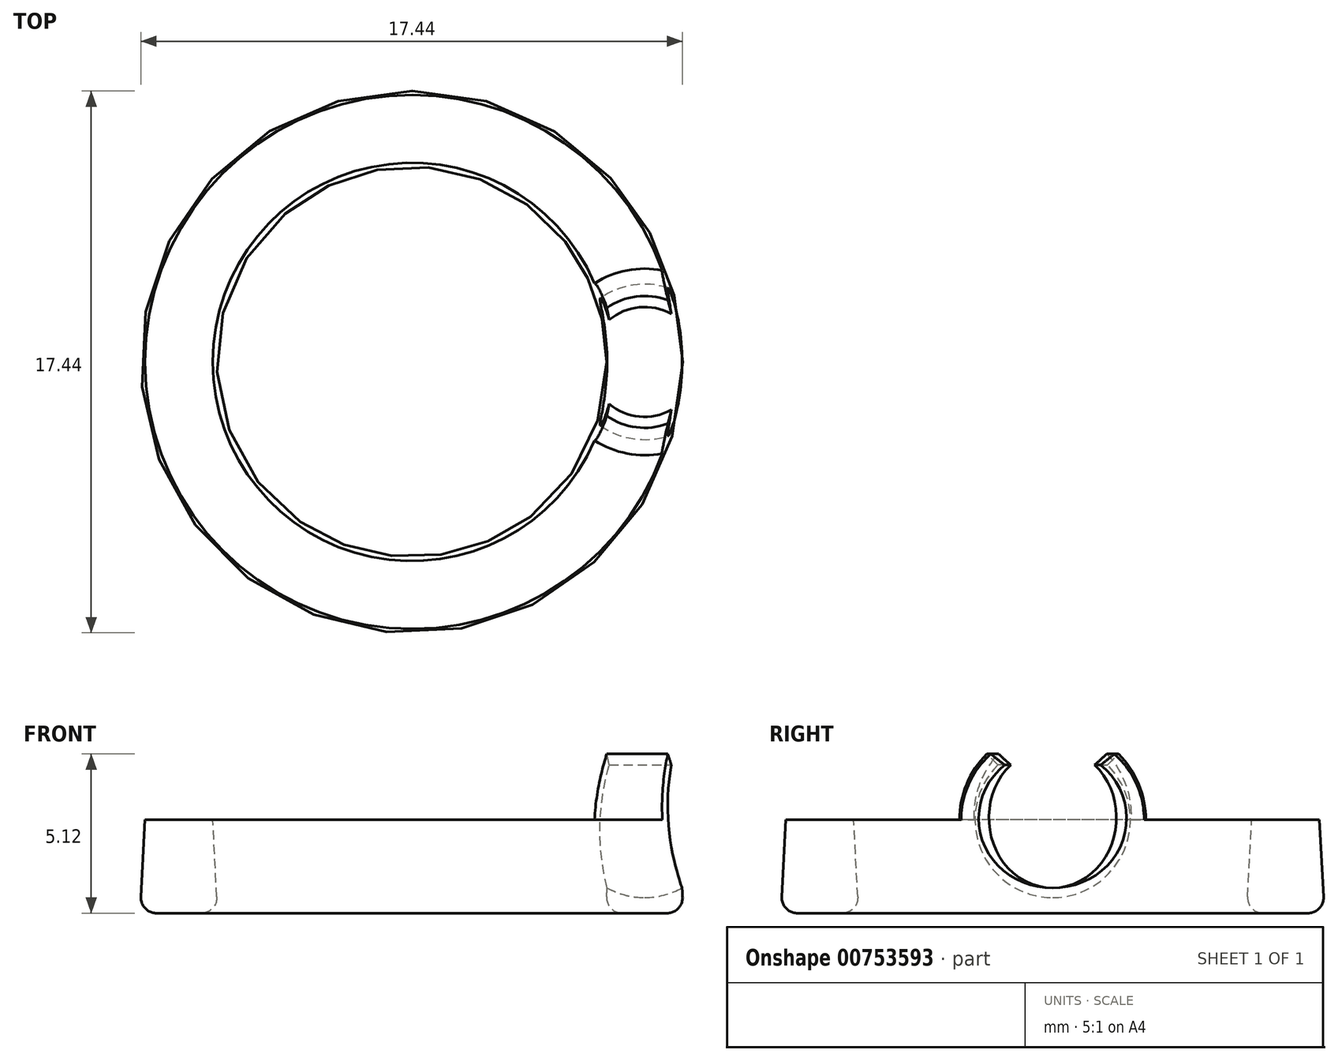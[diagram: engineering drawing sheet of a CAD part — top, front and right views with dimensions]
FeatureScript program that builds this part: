
annotation { "Feature Type Name" : "Feature", "Feature Type Description" : "" }
export const myFeature = defineFeature(function(context is Context, id is Id, definition is map)
    precondition{}
    {
        {
            var Q0;
            Q0=qCreatedBy(makeId("Top.planeOp"),FACE);
            var sketch = newSketch(context, id + "F0", { "sketchPlane" : qUnion([Q0])});
            skCircle(sketch, "E0", {"center": v(0, 0) * mm, "radius": 6.25 * mm});
            skCircle(sketch, "E1", {"center": v(0, 0) * mm, "radius": 8.75 * mm});
            skSolve(sketch);
        }
        {
            var Q0;
            Q0 = qSketchRegion(id + "F0", true);
            extrude(context, id + "F1", {"entities" : qUnion([Q0]), "depth" : 3 * mm, "offsetDistance" : 25 * mm});
        }
        {
            var Q0;
            Q0=qCreatedBy(makeId("Front.planeOp"),FACE);
            var sketch = newSketch(context, id + "F2", { "sketchPlane" : qUnion([Q0])});
            skArc(sketch, "E2", {"start": v(7.5, 5.5) * mm, "mid": v(5, 3) * mm, "end": v(7.5, 0.5) * mm});
            skLineSegment(sketch, "E3", {"start": v(7.5, 5.5) * mm, "end": v(7.5, 0.5) * mm});
            skPoint(sketch, "E4.orphan", {"position": v(8.75, 3) * mm});
            skPoint(sketch, "E5.end.orphan", {"position": v(8.75, 0) * mm});
            skSolve(sketch);
        }
        {
            var Q0;
            Q0 = qSketchRegion(id + "F2", true);
            var Q1;
            Q1=sQuery(id+"F2.wireOp",EDGE,"E3");
            revolve(context, id + "F3", {"operationType" : NewBodyOperationType.REMOVE, "surfaceOperationType" : NewSurfaceOperationType.NEW, "entities" : qUnion([Q0]), "axis" : qUnion([Q1]), "revolveType" : RevolveType.FULL, "oppositeDirection" : true});
        }
        {
            var Q0;
            Q0=qCreatedBy(makeId("Front.planeOp"),FACE);
            var sketch = newSketch(context, id + "F4", { "sketchPlane" : qUnion([Q0])});
            skLineSegment(sketch, "E6", {"start": v(8.75, 0) * mm, "end": v(8.75, 0.27) * mm});
            skArc(sketch, "E7", {"start": v(9.62, 0.88) * mm, "mid": v(10.5, 3) * mm, "end": v(9.62, 5.12) * mm});
            skLineSegment(sketch, "E8", {"start": v(8.75, 0) * mm, "end": v(0, 0) * mm});
            skLineSegment(sketch, "E9", {"start": v(9.27, 4.77) * mm, "end": v(9.62, 5.12) * mm});
            skLineSegment(sketch, "E10", {"start": v(9.27, 1.23) * mm, "end": v(9.62, 0.88) * mm});
            skArc(sketch, "E11.0", {"start": v(9.27, 1.23) * mm, "mid": v(10, 3) * mm, "end": v(9.27, 4.77) * mm});
            skLineSegment(sketch, "E12", {"start": v(7.5, 3) * mm, "end": v(7.5, 0.49) * mm});
            skPoint(sketch, "E13.trimOffspring.end.orphan", {"position": v(8.75, 3) * mm});
            skSolve(sketch);
        }
        {
            var Q0;
            Q0 = qSketchRegion(id + "F4", true);
            var Q1;
            Q1=sQuery(id+"F4.wireOp",EDGE,"E12");
            revolve(context, id + "F5", {"operationType" : NewBodyOperationType.ADD, "surfaceOperationType" : NewSurfaceOperationType.NEW, "entities" : qUnion([Q0]), "axis" : qUnion([Q1]), "revolveType" : RevolveType.FULL});
        }
        {
            var Q0;
            Q0=qCreatedBy(makeId("Front.planeOp"),FACE);
            var sketch = newSketch(context, id + "F6", { "sketchPlane" : qUnion([Q0])});
            skLineSegment(sketch, "E14", {"start": v(0, 0) * mm, "end": v(0, 11.1) * mm});
            skSolve(sketch);
        }
        {
            var Q0;
            Q0=qCreatedBy(makeId("Front.planeOp"),FACE);
            var sketch = newSketch(context, id + "F7", { "sketchPlane" : qUnion([Q0])});
            skLineSegment(sketch, "E15", {"start": v(0, 0) * mm, "end": v(0, 7.84) * mm});
            skSolve(sketch);
        }
        {
            var Q0;
            Q0=makeQuery(id+"F1.opExtrude","CAP_FACE",FACE,{"disambiguationData":[OSD([sQuery(id+"F0.wireOp",EDGE,"E0"),sQuery(id+"F0.wireOp",EDGE,"E1")])],"isStart":true});
            var sketch = newSketch(context, id + "F8", { "sketchPlane" : qUnion([Q0])});
            skCircle(sketch, "E16", {"center": v(0, 0) * mm, "radius": 8.75 * mm});
            skCircle(sketch, "E17", {"center": v(0, 0) * mm, "radius": 6.25 * mm});
            skCircle(sketch, "E18", {"center": v(0, 0) * mm, "radius": 11 * mm});
            skSolve(sketch);
        }
        {
            var Q0;
            Q0=makeQuery(id+"F8.imprint","IMPRINT",FACE,{"disambiguationData":[TD([[makeQuery(id+"F8.imprint","IMPRINT",EDGE,{"derivedFrom":sQuery(id+"F8.wireOp",EDGE,"E16")}),1.0]])]});
            var Q1;
            Q1=makeQuery(id+"F8.imprint","IMPRINT",FACE,{"disambiguationData":[TD([[makeQuery(id+"F8.imprint","IMPRINT",EDGE,{"derivedFrom":sQuery(id+"F8.wireOp",EDGE,"E17")}),-1.0]])]});
            extrude(context, id + "F9", {"entities" : qUnion([Q0, Q1]), "operationType" : NewBodyOperationType.REMOVE, "oppositeDirection" : true, "depth" : 6 * mm, "offsetDistance" : 25 * mm, "hasDraft" : true, "draftAngle" : 3 * degree});
        }
        {
            var Q0;
            Q0=makeQuery(id+"F9.boolean.opBoolean","MERGE",EDGE,{"derivedFrom":[makeQuery(id+"F1.opExtrude","CAP_EDGE",EDGE,{"disambiguationData":[OSD([sQuery(id+"F0.wireOp",EDGE,"E1")])],"isStart":true}),makeQuery(id+"F9.opExtrude","CAP_EDGE",EDGE,{"disambiguationData":[OSD([sQuery(id+"F8.wireOp",EDGE,"E16")])],"isStart":true})]});
            var Q1;
            Q1=makeQuery(id+"F9.boolean.opBoolean","MERGE",EDGE,{"derivedFrom":[makeQuery(id+"F1.opExtrude","CAP_EDGE",EDGE,{"disambiguationData":[OSD([sQuery(id+"F0.wireOp",EDGE,"E0")])],"isStart":true}),makeQuery(id+"F9.opExtrude","CAP_EDGE",EDGE,{"disambiguationData":[OSD([sQuery(id+"F8.wireOp",EDGE,"E17")])],"isStart":true})]});
            fillet(context, id + "F10", {"entities" : qUnion([Q0, Q1]), "radius" : 0.5 * mm, "tangentPropagation" : true, "allowEdgeOverflow" : false});
        }
    });
